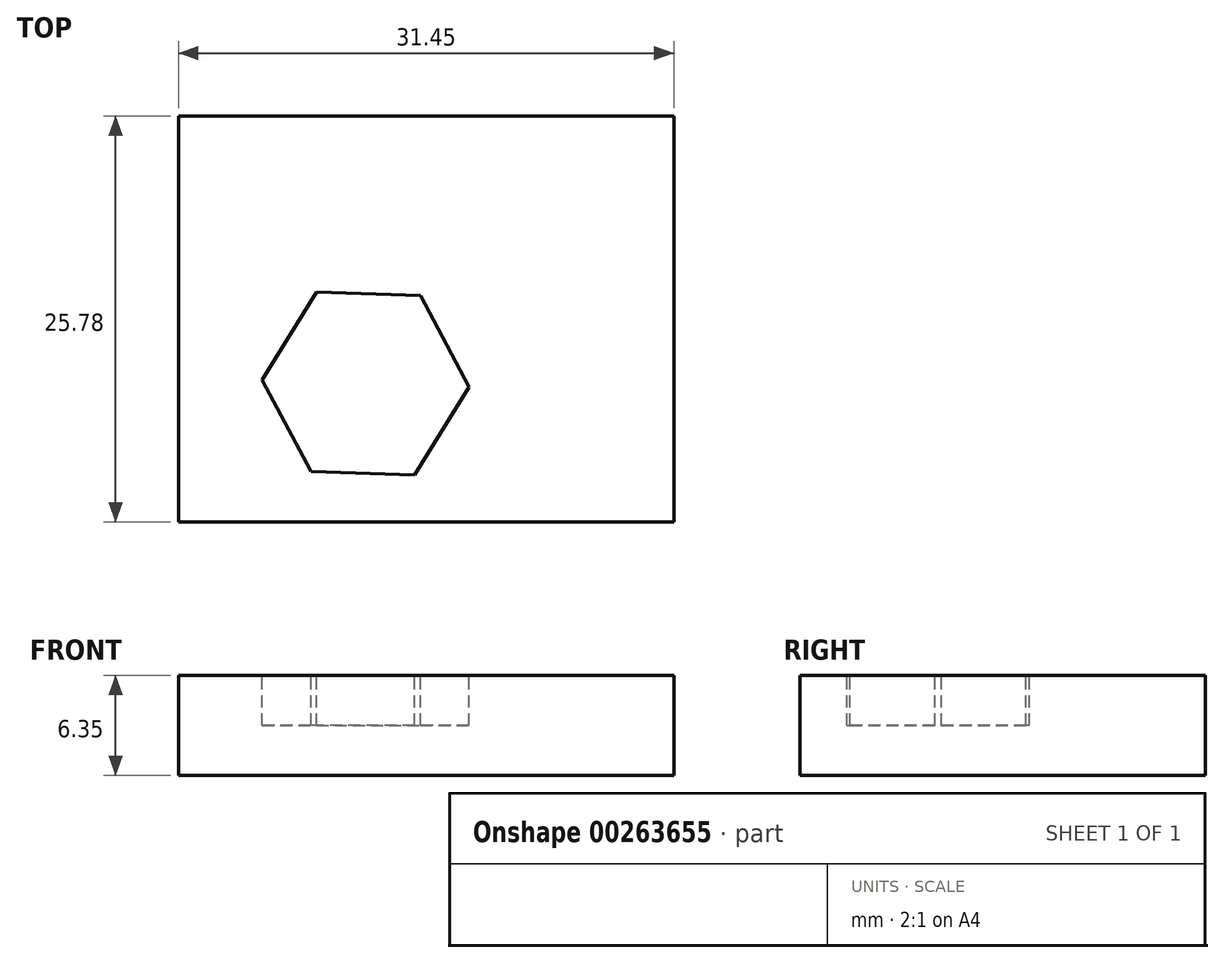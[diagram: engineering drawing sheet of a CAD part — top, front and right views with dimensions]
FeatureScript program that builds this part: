
annotation { "Feature Type Name" : "Feature", "Feature Type Description" : "" }
export const myFeature = defineFeature(function(context is Context, id is Id, definition is map)
    precondition{}
    {
        {
            var Q0;
            Q0=qCreatedBy(makeId("Top.planeOp"),FACE);
            var sketch = newSketch(context, id + "F0", { "sketchPlane" : qUnion([Q0])});
            skLineSegment(sketch, "E0.bottom", {"start": v(0, 0) * mm, "end": v(31.45, 0) * mm});
            skLineSegment(sketch, "E0.top", {"start": v(0, 25.78) * mm, "end": v(31.45, 25.78) * mm});
            skLineSegment(sketch, "E0.left", {"start": v(0, 0) * mm, "end": v(0, 25.78) * mm});
            skLineSegment(sketch, "E0.right", {"start": v(31.45, 0) * mm, "end": v(31.45, 25.78) * mm});
            skSolve(sketch);
        }
        {
            var Q0;
            Q0 = qSketchRegion(id + "F0", true);
            extrude(context, id + "F1", {"entities" : qUnion([Q0]), "depth" : 6.35 * mm});
        }
        {
            var Q0;
            Q0=makeQuery(id+"F1.opExtrude","CAP_FACE",FACE,{"disambiguationData":[OSD([sQuery(id+"F0.wireOp",EDGE,"E0.bottom"),sQuery(id+"F0.wireOp",EDGE,"E0.top"),sQuery(id+"F0.wireOp",EDGE,"E0.left"),sQuery(id+"F0.wireOp",EDGE,"E0.right")])],"isStart":false});
            var sketch = newSketch(context, id + "F2", { "sketchPlane" : qUnion([Q0])});
            skCircle(sketch, "E1.cCircle", {"center": v(11.88, 8.79) * mm, "radius": 5.7 * mm, "construction": true});
            skLineSegment(sketch, "E1.0", {"start": v(15.35, 14.37) * mm, "end": v(18.45, 8.57) * mm});
            skLineSegment(sketch, "E1.1", {"start": v(18.45, 8.57) * mm, "end": v(14.98, 2.99) * mm});
            skLineSegment(sketch, "E1.2", {"start": v(14.98, 2.99) * mm, "end": v(8.4, 3.2) * mm});
            skLineSegment(sketch, "E1.3", {"start": v(8.4, 3.2) * mm, "end": v(5.3, 9) * mm});
            skLineSegment(sketch, "E1.4", {"start": v(5.3, 9) * mm, "end": v(8.78, 14.6) * mm});
            skLineSegment(sketch, "E1.5", {"start": v(8.78, 14.6) * mm, "end": v(15.35, 14.37) * mm});
            skPoint(sketch, "E1.0.midPoint", {"position": v(16.9, 11.47) * mm});
            skSolve(sketch);
        }
        {
            var Q0;
            Q0 = qSketchRegion(id + "F2", true);
            extrude(context, id + "F3", {"entities" : qUnion([Q0]), "operationType" : NewBodyOperationType.REMOVE, "oppositeDirection" : true, "depth" : 3.17 * mm});
        }
    });
